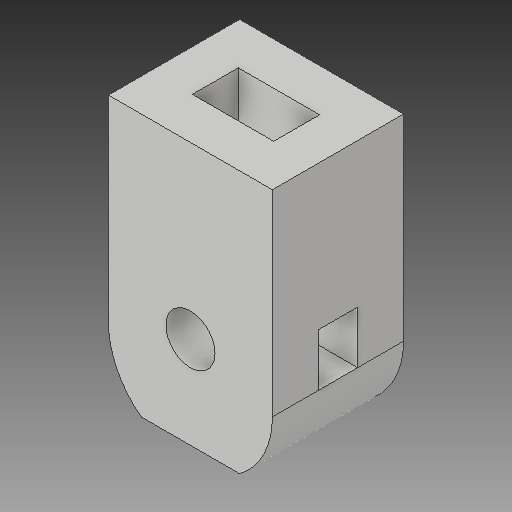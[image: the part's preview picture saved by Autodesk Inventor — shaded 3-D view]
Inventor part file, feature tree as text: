
AUTODESK INVENTOR PART (.ipt)
format: ipt  version: 2019 (Build 230136000, 136)  size: 162,304 bytes
history: native  units: mm
features: sketch x8, extrude x5, plane x1, hole x1, projected_geometry x1
ambient origin geometry x8: Origin, YZ Plane, XZ Plane, XY Plane, X Axis, Y Axis, Z Axis, Center Point
bodies: Solid1 (feature_tree)
feature tree (16):
  extrude  "Extrusion1"  Depth=30.0mm
  plane  "Work Plane1"
  extrude  "Extrusion2"  Depth=12.5mm
  sketch  "Sketch3"  dims[d4=12.5mm d5=12.5mm]
  sketch  "Sketch4"  dims[d6=20.0mm d7=0.0mm d8=10.0mm]
  extrude  "Extrusion3"  Depth=12.5mm
  hole  "Hole1"  [1 undecoded]
  extrude  "Extrusion4"  Depth=7.0mm TaperAngle=0.0deg
  extrude  "Extrusion5"  Depth=6.0mm
  sketch  "Sketch1"  dims[d0=25.0mm d1=30.0mm]
  sketch  "Sketch2"  dims[d2=30.0mm d3=12.5mm]
  projected_geometry  "Projected Loop1"
  sketch  "Sketch6"  dims[d9=12.4mm d10=7.0mm d11=0.0mm]
  sketch  "Sketch7"  dims[d12=30.0mm d13=0.0mm]
  sketch  "Sketch8"  dims[d14=7.5mm d15=6.0mm d16=4.0mm d17=2.0mm d18=90.0deg d19=8.0mm d20=0.0mm d21=6.0mm]
  sketch  "Sketch9"  dims[d22=8.0mm d23=7.0mm d24=0.0mm d25=25.0mm d26=0.0mm d27=26.0mm d28=12.5mm d29=10.0mm d30=5.0mm d31=20.0mm d32=20.0mm d33=0.0mm]
note: 1 required parameter value undecoded (feature->parameter linkage not recoverable at this tier; creation-order binding heuristic only, values carry confidence <= 0.55)
